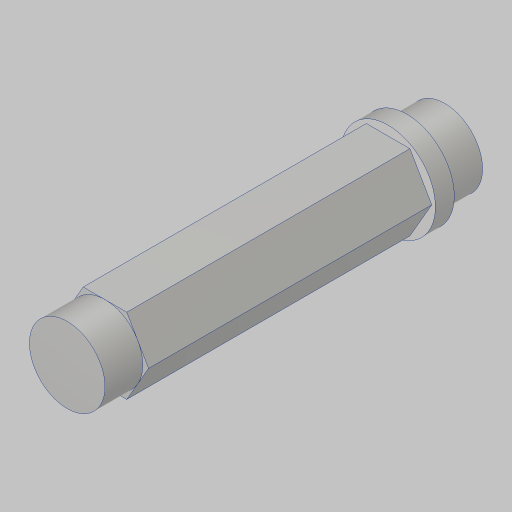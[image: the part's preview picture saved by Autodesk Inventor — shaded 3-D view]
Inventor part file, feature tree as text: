
AUTODESK INVENTOR PART (.ipt)
format: ipt  version: 2023.5 (Build 275446000, 446)  size: 146,432 bytes
history: native  units: in
note: dims shown in document units (in); Inventor stores cm internally (conversion verified against a paired STEP export)
features: extrude x5, sketch x5, projected_geometry x4
ambient origin geometry x8: Origin, YZ Plane, XZ Plane, XY Plane, X Axis, Y Axis, Z Axis, Center Point
bodies: Solid1 (feature_tree)
feature tree (14):
  extrude  "Extrusion1"  Depth=3.5625in TaperAngle=0.0deg
  extrude  "Extrusion2"  Depth=2.125in TaperAngle=0.0deg
  extrude  "Extrusion3"  Depth=0.25in TaperAngle=0.0deg
  extrude  "Extrusion4"  Depth=0.25in TaperAngle=0.0deg
  extrude  "Extrusion5"  Depth=0.25in TaperAngle=0.0deg
  sketch  "Sketch1"  dims[d0=0.625in d1=3.5625in d2=0.0in]
  sketch  "Sketch2"  dims[d3=0.5in d4=2.125in d5=0.0in]
  projected_geometry  "Projected Loop1"
  sketch  "Sketch3"  dims[d6=0.5in d7=0.25in d8=0.0in]
  projected_geometry  "Projected Loop2"
  sketch  "Sketch4"  dims[d9=2.5in d10=0.25in d11=0.0in]
  sketch  "Sketch5"  dims[d12=0.5in d13=0.25in d14=0.0in]
  projected_geometry  "Project Cut Edges1"
  projected_geometry  "Project Cut Edges2"
